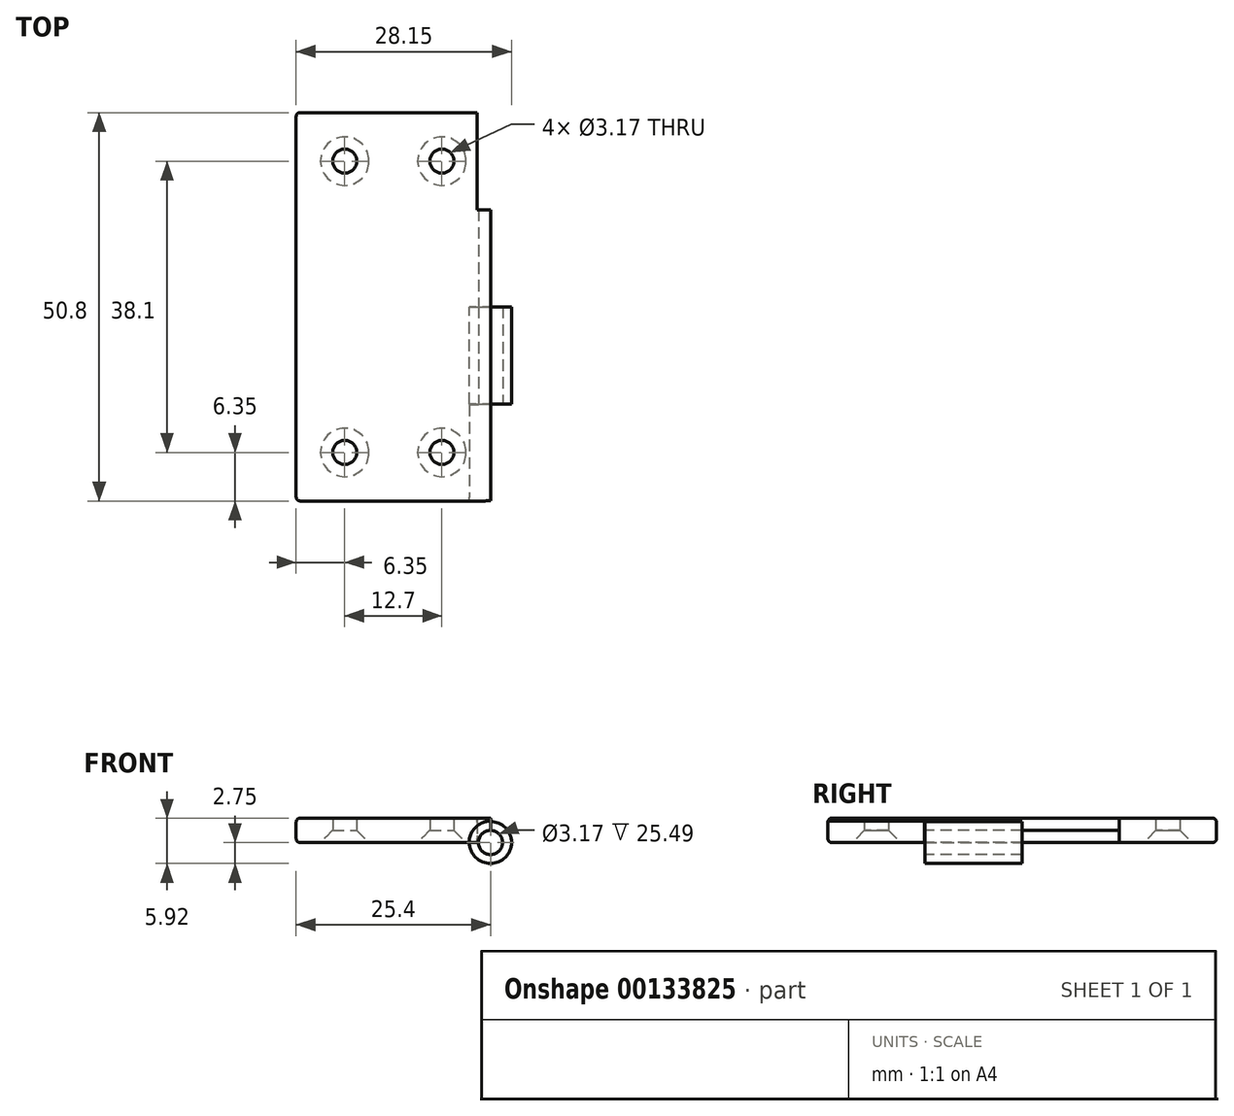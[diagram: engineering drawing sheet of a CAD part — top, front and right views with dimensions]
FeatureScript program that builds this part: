
annotation { "Feature Type Name" : "Feature", "Feature Type Description" : "" }
export const myFeature = defineFeature(function(context is Context, id is Id, definition is map)
    precondition{}
    {
        {
            var Q0;
            Q0=qCreatedBy(makeId("Top.planeOp"),FACE);
            var sketch = newSketch(context, id + "F0", { "sketchPlane" : qUnion([Q0])});
            skLineSegment(sketch, "E0.bottom", {"start": v(-108.07, 23.2) * mm, "end": v(-101.72, 23.2) * mm});
            skLineSegment(sketch, "E0.top", {"start": v(-108.07, -27.6) * mm, "end": v(-101.72, -27.6) * mm});
            skLineSegment(sketch, "E0.left", {"start": v(-108.07, 23.2) * mm, "end": v(-108.07, 16.85) * mm});
            skLineSegment(sketch, "E0.right", {"start": v(-82.67, 23.2) * mm, "end": v(-82.67, 10.5) * mm});
            skLineSegment(sketch, "E1", {"start": v(-82.67, -2.2) * mm, "end": v(-82.67, -14.9) * mm});
            skLineSegment(sketch, "E2", {"start": v(-82.67, 10.5) * mm, "end": v(-82.67, -2.2) * mm});
            skLineSegment(sketch, "E3", {"start": v(-82.67, -14.9) * mm, "end": v(-82.67, -21.25) * mm});
            skLineSegment(sketch, "E4.left", {"start": v(-82.67, 23.2) * mm, "end": v(-82.67, 16.85) * mm});
            skLineSegment(sketch, "E5.bottom", {"start": v(-79.92, -2.2) * mm, "end": v(-84.42, -2.2) * mm});
            skLineSegment(sketch, "E5.top", {"start": v(-79.92, -14.9) * mm, "end": v(-84.42, -14.9) * mm});
            skLineSegment(sketch, "E5.left", {"start": v(-79.92, -2.2) * mm, "end": v(-79.92, -14.9) * mm});
            skLineSegment(sketch, "E5.right", {"start": v(-84.42, -2.2) * mm, "end": v(-84.42, -14.9) * mm});
            skLineSegment(sketch, "E6.bottom", {"start": v(-79.92, 23.2) * mm, "end": v(-84.42, 23.2) * mm});
            skLineSegment(sketch, "E6.top", {"start": v(-79.92, 10.5) * mm, "end": v(-84.42, 10.5) * mm});
            skLineSegment(sketch, "E6.left", {"start": v(-79.92, 23.2) * mm, "end": v(-79.92, 10.5) * mm});
            skLineSegment(sketch, "E6.right", {"start": v(-84.42, 23.2) * mm, "end": v(-84.42, 10.5) * mm});
            skLineSegment(sketch, "E7", {"start": v(-95.37, 23.2) * mm, "end": v(-89.02, 23.2) * mm});
            skLineSegment(sketch, "E8", {"start": v(-101.72, 23.2) * mm, "end": v(-95.37, 23.2) * mm});
            skLineSegment(sketch, "E9", {"start": v(-108.07, -2.2) * mm, "end": v(-108.07, -14.9) * mm});
            skLineSegment(sketch, "E10", {"start": v(-108.07, 10.5) * mm, "end": v(-108.07, -2.2) * mm});
            skLineSegment(sketch, "E11", {"start": v(-108.07, 16.85) * mm, "end": v(-108.07, 10.5) * mm});
            skLineSegment(sketch, "E12", {"start": v(-108.07, -14.9) * mm, "end": v(-108.07, -21.25) * mm});
            skLineSegment(sketch, "E13", {"start": v(-108.07, -21.25) * mm, "end": v(-108.07, -27.6) * mm});
            skLineSegment(sketch, "E14", {"start": v(-95.37, -27.6) * mm, "end": v(-89.02, -27.6) * mm});
            skLineSegment(sketch, "E15", {"start": v(-101.72, -27.6) * mm, "end": v(-95.37, -27.6) * mm});
            skLineSegment(sketch, "E16", {"start": v(-89.02, -27.6) * mm, "end": v(-82.67, -27.6) * mm});
            skLineSegment(sketch, "E17", {"start": v(-82.67, -21.25) * mm, "end": v(-82.67, -27.6) * mm});
            skLineSegment(sketch, "E18", {"start": v(-89.02, 23.2) * mm, "end": v(-82.67, 23.2) * mm});
            skLineSegment(sketch, "E19", {"start": v(-82.67, 16.85) * mm, "end": v(-82.67, 10.5) * mm});
            skPoint(sketch, "E20", {"position": v(-101.72, 16.85) * mm});
            skPoint(sketch, "E21", {"position": v(-89.02, 16.85) * mm});
            skPoint(sketch, "E21.positionSnap0", {"position": v(-84.42, 16.85) * mm});
            skPoint(sketch, "E22", {"position": v(-101.72, -21.25) * mm});
            skPoint(sketch, "E23", {"position": v(-89.02, -21.25) * mm});
            skSolve(sketch);
        }
        {
            var Q0;
            Q0=makeQuery(id+"F0.imprint","IMPRINT",FACE,{"disambiguationData":[TD([[makeQuery(id+"F0.imprint","IMPRINT",EDGE,{"derivedFrom":sQuery(id+"F0.wireOp",EDGE,"E0.bottom")}),-1.0]])]});
            var Q1;
            {var subQ0=sQuery(id+"F0.wireOp",EDGE,"E4.left");Q1=makeQuery(id+"F0.imprint","IMPRINT",FACE,{"disambiguationData":[TD([[makeQuery(id+"F0.imprint","IMPRINT",EDGE,{"derivedFrom":subQ0}),-1.0]])]});}
            var Q2;
            {var subQ0=sQuery(id+"F0.wireOp",EDGE,"E1");Q2=makeQuery(id+"F0.imprint","IMPRINT",FACE,{"disambiguationData":[TD([[makeQuery(id+"F0.imprint","IMPRINT",EDGE,{"derivedFrom":subQ0}),-1.0]])]});}
            extrude(context, id + "F1", {"entities" : qUnion([Q0, Q1, Q2]), "depth" : 3.17 * mm});
        }
        {
            var Q0;
            {var subQ0=sQuery(id+"F0.wireOp",EDGE,"E4.left");Q0=makeQuery(id+"F0.imprint","IMPRINT",FACE,{"disambiguationData":[TD([[makeQuery(id+"F0.imprint","IMPRINT",EDGE,{"derivedFrom":subQ0}),1.0]])]});}
            var Q1;
            {var subQ0=sQuery(id+"F0.wireOp",EDGE,"E1");Q1=makeQuery(id+"F0.imprint","IMPRINT",FACE,{"disambiguationData":[TD([[makeQuery(id+"F0.imprint","IMPRINT",EDGE,{"derivedFrom":subQ0}),1.0]])]});}
            var Q2;
            Q2=sQuery(id+"F0.wireOp",EDGE,"E4.left");
            revolve(context, id + "F2", {"operationType" : NewBodyOperationType.ADD, "entities" : qUnion([Q0, Q1]), "axis" : qUnion([Q2]), "revolveType" : RevolveType.FULL});
        }
        {
            var Q0;
            Q0=qCreatedBy(makeId("Front.planeOp"),FACE);
            cPlane(context, id + "F3", {"entities" : qUnion([Q0]), "cplaneType" : CPlaneType.OFFSET, "offset" : 50.8 * mm, "width" : 152.4 * mm, "height" : 152.4 * mm});
        }
        {
            var Q0;
            Q0=qCreatedBy(id+"F3.planeOp",FACE);
            var sketch = newSketch(context, id + "F4", { "sketchPlane" : qUnion([Q0])});
            skPoint(sketch, "E24", {"position": v(-82.67, 0) * mm});
            skSolve(sketch);
        }
        {
            var Q0;
            Q0=sQuery(id+"F4.wireOp",VERTEX,"E24");
            var Q1;
            Q1=makeQuery(id+"F1.opExtrude","SWEPT_BODY",BODY,{"disambiguationData":[OSD([sQuery(id+"F0.wireOp",EDGE,"E0.bottom"),sQuery(id+"F0.wireOp",EDGE,"E0.top"),sQuery(id+"F0.wireOp",EDGE,"E0.left"),sQuery(id+"F0.wireOp",EDGE,"E2"),sQuery(id+"F0.wireOp",EDGE,"E3"),sQuery(id+"F0.wireOp",EDGE,"E4.left"),sQuery(id+"F0.wireOp",EDGE,"E1"),sQuery(id+"F0.wireOp",EDGE,"E6.bottom")])]});
            hole(context, id + "F5", {"style" : HoleStyle.SIMPLE, "endStyle" : HoleEndStyle.THROUGH, "holeDiameter" : 3.17 * mm, "locations" : qUnion([Q0]), "scope" : qUnion([Q1]), "isTappedThrough" : true});
        }
        {
            var Q0;
            Q0=sQuery(id+"F0.wireOp",VERTEX,"E20");
            var Q1;
            Q1=sQuery(id+"F0.wireOp",VERTEX,"E21");
            var Q2;
            Q2=sQuery(id+"F0.wireOp",VERTEX,"E23");
            var Q3;
            Q3=sQuery(id+"F0.wireOp",VERTEX,"E22");
            var Q4;
            Q4=makeQuery(id+"F1.opExtrude","SWEPT_BODY",BODY,{"disambiguationData":[OSD([sQuery(id+"F0.wireOp",EDGE,"E0.bottom"),sQuery(id+"F0.wireOp",EDGE,"E0.top"),sQuery(id+"F0.wireOp",EDGE,"E0.left"),sQuery(id+"F0.wireOp",EDGE,"E2"),sQuery(id+"F0.wireOp",EDGE,"E3"),sQuery(id+"F0.wireOp",EDGE,"E4.left"),sQuery(id+"F0.wireOp",EDGE,"E1"),sQuery(id+"F0.wireOp",EDGE,"E7"),sQuery(id+"F0.wireOp",EDGE,"E8"),sQuery(id+"F0.wireOp",EDGE,"E9"),sQuery(id+"F0.wireOp",EDGE,"E10"),sQuery(id+"F0.wireOp",EDGE,"E11"),sQuery(id+"F0.wireOp",EDGE,"E12"),sQuery(id+"F0.wireOp",EDGE,"E13"),sQuery(id+"F0.wireOp",EDGE,"E14"),sQuery(id+"F0.wireOp",EDGE,"E15"),sQuery(id+"F0.wireOp",EDGE,"E16"),sQuery(id+"F0.wireOp",EDGE,"E17"),sQuery(id+"F0.wireOp",EDGE,"E18"),sQuery(id+"F0.wireOp",EDGE,"E19")])]});
            hole(context, id + "F6", {"style" : HoleStyle.C_SINK, "endStyle" : HoleEndStyle.THROUGH, "oppositeDirection" : true, "holeDiameter" : 3.17 * mm, "cSinkDiameter" : 6.35 * mm, "cSinkAngle" : 90 * degree, "locations" : qUnion([Q0, Q1, Q2, Q3]), "scope" : qUnion([Q4]), "isTappedThrough" : true});
        }
        {
            var Q0;
            Q0=makeQuery(id+"F1.opExtrude","CAP_EDGE",EDGE,{"disambiguationData":[OSD([sQuery(id+"F0.wireOp",EDGE,"E0.left"),sQuery(id+"F0.wireOp",EDGE,"E9"),sQuery(id+"F0.wireOp",EDGE,"E10"),sQuery(id+"F0.wireOp",EDGE,"E11"),sQuery(id+"F0.wireOp",EDGE,"E12"),sQuery(id+"F0.wireOp",EDGE,"E13")])],"isStart":true});
            var Q1;
            Q1=makeQuery(id+"F1.opExtrude","CAP_EDGE",EDGE,{"disambiguationData":[OSD([sQuery(id+"F0.wireOp",EDGE,"E0.bottom"),sQuery(id+"F0.wireOp",EDGE,"E7"),sQuery(id+"F0.wireOp",EDGE,"E8"),sQuery(id+"F0.wireOp",EDGE,"E18")])],"isStart":true});
            var Q2;
            Q2=makeQuery(id+"F1.opExtrude","CAP_EDGE",EDGE,{"disambiguationData":[OSD([sQuery(id+"F0.wireOp",EDGE,"E0.top"),sQuery(id+"F0.wireOp",EDGE,"E14"),sQuery(id+"F0.wireOp",EDGE,"E15"),sQuery(id+"F0.wireOp",EDGE,"E16")])],"isStart":true});
            var Q3;
            Q3=makeQuery(id+"F1.opExtrude","CAP_EDGE",EDGE,{"disambiguationData":[OSD([sQuery(id+"F0.wireOp",EDGE,"E0.left"),sQuery(id+"F0.wireOp",EDGE,"E9"),sQuery(id+"F0.wireOp",EDGE,"E10"),sQuery(id+"F0.wireOp",EDGE,"E11"),sQuery(id+"F0.wireOp",EDGE,"E12"),sQuery(id+"F0.wireOp",EDGE,"E13")])],"isStart":false});
            var Q4;
            Q4=makeQuery(id+"F1.opExtrude","CAP_EDGE",EDGE,{"disambiguationData":[OSD([sQuery(id+"F0.wireOp",EDGE,"E0.bottom"),sQuery(id+"F0.wireOp",EDGE,"E7"),sQuery(id+"F0.wireOp",EDGE,"E8"),sQuery(id+"F0.wireOp",EDGE,"E18")])],"isStart":false});
            var Q5;
            Q5=makeQuery(id+"F1.opExtrude","CAP_EDGE",EDGE,{"disambiguationData":[OSD([sQuery(id+"F0.wireOp",EDGE,"E0.top"),sQuery(id+"F0.wireOp",EDGE,"E14"),sQuery(id+"F0.wireOp",EDGE,"E15"),sQuery(id+"F0.wireOp",EDGE,"E16")])],"isStart":false});
            var Q6;
            Q6=makeQuery(id+"F1.opExtrude","SWEPT_EDGE",EDGE,{"disambiguationData":[OSD([sQuery(id+"F0.wireOp",EDGE,"E0.bottom"),sQuery(id+"F0.wireOp",EDGE,"E0.left")])]});
            var Q7;
            Q7=makeQuery(id+"F1.opExtrude","SWEPT_EDGE",EDGE,{"disambiguationData":[OSD([sQuery(id+"F0.wireOp",EDGE,"E0.top"),sQuery(id+"F0.wireOp",EDGE,"E13")])]});
            fillet(context, id + "F7", {"entities" : qUnion([Q0, Q1, Q2, Q3, Q4, Q5, Q6, Q7]), "radius" : 0.5 * mm, "tangentPropagation" : true, "allowEdgeOverflow" : false});
        }
        {
            var Q0;
            Q0=qCreatedBy(id+"F3.planeOp",FACE);
            var sketch = newSketch(context, id + "F8", { "sketchPlane" : qUnion([Q0])});
            skCircle(sketch, "E25", {"center": v(-82.66, 0) * mm, "radius": 0.64 * mm});
            skSolve(sketch);
        }
        {
            var Q0;
            Q0=makeQuery(id+"F8.imprint","IMPRINT",FACE,{"disambiguationData":[TD([[makeQuery(id+"F8.imprint","IMPRINT",EDGE,{"derivedFrom":sQuery(id+"F8.wireOp",EDGE,"E25")}),1.0]])]});
            extrude(context, id + "F9", {"entities" : qUnion([Q0]), "operationType" : NewBodyOperationType.ADD, "oppositeDirection" : true, "depth" : 35.81 * mm});
        }
        {
            var Q0;
            Q0=makeQuery(id+"F9.opExtrude","SWEPT_BODY",BODY,{"disambiguationData":[OSD([sQuery(id+"F8.wireOp",EDGE,"E25")])]});
            var Q1;
            Q1=makeQuery(id+"F1.opExtrude","SWEPT_BODY",BODY,{"disambiguationData":[OSD([sQuery(id+"F0.wireOp",EDGE,"E0.bottom"),sQuery(id+"F0.wireOp",EDGE,"E0.top"),sQuery(id+"F0.wireOp",EDGE,"E0.left"),sQuery(id+"F0.wireOp",EDGE,"E2"),sQuery(id+"F0.wireOp",EDGE,"E3"),sQuery(id+"F0.wireOp",EDGE,"E4.left"),sQuery(id+"F0.wireOp",EDGE,"E1"),sQuery(id+"F0.wireOp",EDGE,"E7"),sQuery(id+"F0.wireOp",EDGE,"E8"),sQuery(id+"F0.wireOp",EDGE,"E9"),sQuery(id+"F0.wireOp",EDGE,"E10"),sQuery(id+"F0.wireOp",EDGE,"E11"),sQuery(id+"F0.wireOp",EDGE,"E12"),sQuery(id+"F0.wireOp",EDGE,"E13"),sQuery(id+"F0.wireOp",EDGE,"E14"),sQuery(id+"F0.wireOp",EDGE,"E15"),sQuery(id+"F0.wireOp",EDGE,"E16"),sQuery(id+"F0.wireOp",EDGE,"E17"),sQuery(id+"F0.wireOp",EDGE,"E18"),sQuery(id+"F0.wireOp",EDGE,"E19")])]});
            var Q2;
            Q2=makeQuery(id+"F9.opExtrude","SWEPT_FACE",FACE,{"disambiguationData":[OSD([sQuery(id+"F8.wireOp",EDGE,"E25")])]});
            booleanBodies(context, id + "F10", {"operationType" : BooleanOperationType.SUBTRACTION, "tools" : qUnion([Q0]), "targets" : qUnion([Q1]), "offset" : true, "entitiesToOffset" : qUnion([Q2]), "offsetDistance" : 2.16 * mm});
        }
    });
